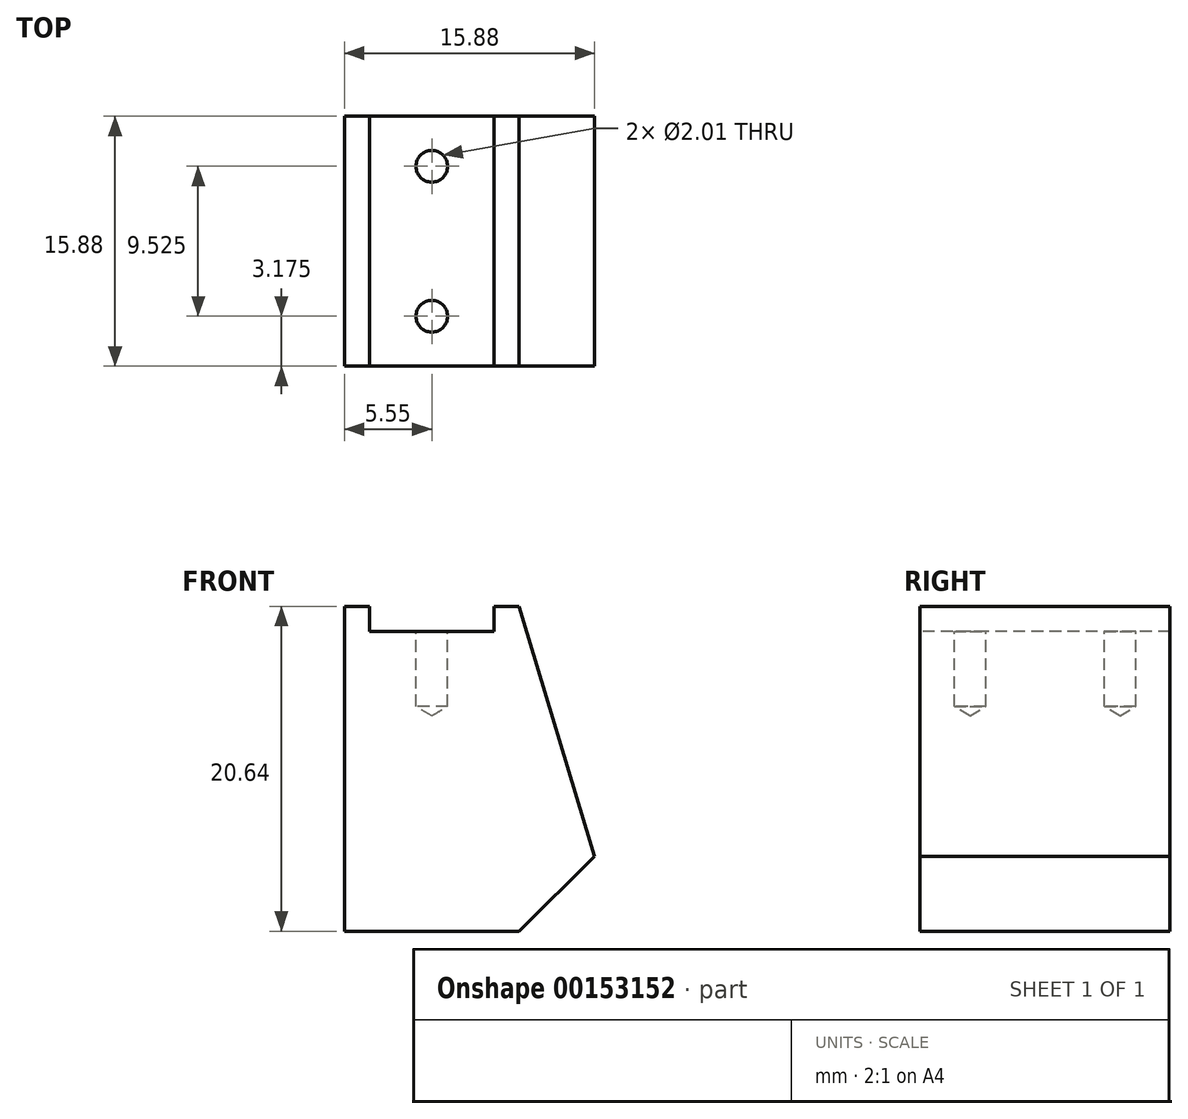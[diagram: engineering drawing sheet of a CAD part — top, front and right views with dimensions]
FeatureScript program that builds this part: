
annotation { "Feature Type Name" : "Feature", "Feature Type Description" : "" }
export const myFeature = defineFeature(function(context is Context, id is Id, definition is map)
    precondition{}
    {
        {
            var Q0;
            Q0=qCreatedBy(makeId("Top.planeOp"),FACE);
            var sketch = newSketch(context, id + "F0", { "sketchPlane" : qUnion([Q0])});
            skLineSegment(sketch, "E0.rect.bottom", {"start": v(7.94, -7.94) * mm, "end": v(-7.94, -7.94) * mm});
            skLineSegment(sketch, "E0.rect.top", {"start": v(7.94, 7.94) * mm, "end": v(-7.94, 7.94) * mm});
            skLineSegment(sketch, "E0.rect.left", {"start": v(7.94, -7.94) * mm, "end": v(7.94, 7.94) * mm});
            skLineSegment(sketch, "E0.rect.right", {"start": v(-7.94, -7.94) * mm, "end": v(-7.94, 7.94) * mm});
            skPoint(sketch, "E0.rect.middle", {"position": v(0, 0) * mm});
            skSolve(sketch);
        }
        {
            var Q0;
            Q0=qSketchRegion(id+"F0",true);
            extrude(context, id + "F1", {"entities" : qUnion([Q0]), "oppositeDirection" : true, "depth" : 20.64 * mm});
        }
        {
            var Q0;
            Q0=makeQuery(id+"F1.opExtrude","CAP_FACE",FACE,{"disambiguationData":[OSD([sQuery(id+"F0.wireOp",EDGE,"E0.rect.bottom"),sQuery(id+"F0.wireOp",EDGE,"E0.rect.top"),sQuery(id+"F0.wireOp",EDGE,"E0.rect.left"),sQuery(id+"F0.wireOp",EDGE,"E0.rect.right")])],"isStart":true});
            var sketch = newSketch(context, id + "F2", { "sketchPlane" : qUnion([Q0])});
            skLineSegment(sketch, "E1.bottom", {"start": v(-6.35, 7.94) * mm, "end": v(1.57, 7.94) * mm});
            skLineSegment(sketch, "E1.top", {"start": v(-6.35, -7.94) * mm, "end": v(1.57, -7.94) * mm});
            skLineSegment(sketch, "E1.left", {"start": v(-6.35, 7.94) * mm, "end": v(-6.35, -7.94) * mm});
            skLineSegment(sketch, "E1.right", {"start": v(1.57, 7.94) * mm, "end": v(1.57, -7.94) * mm});
            skSolve(sketch);
        }
        {
            var Q0;
            Q0=qSketchRegion(id+"F2",true);
            extrude(context, id + "F3", {"entities" : qUnion([Q0]), "operationType" : NewBodyOperationType.REMOVE, "oppositeDirection" : true, "depth" : 1.59 * mm});
        }
        {
            var Q0;
            Q0=makeQuery(id+"F1.opExtrude","SWEPT_BODY",BODY,{"disambiguationData":[OSD([sQuery(id+"F0.wireOp",EDGE,"E0.rect.bottom"),sQuery(id+"F0.wireOp",EDGE,"E0.rect.top"),sQuery(id+"F0.wireOp",EDGE,"E0.rect.left"),sQuery(id+"F0.wireOp",EDGE,"E0.rect.right")])]});
            var Q1;
            {var subQ0=sQuery(id+"F0.wireOp",EDGE,"E0.rect.bottom");var subQ1=sQuery(id+"F0.wireOp",EDGE,"E0.rect.left");Q1=makeQuery(id+"F3.boolean.opBoolean","SPLIT",EDGE,{"disambiguationData":[TD([makeQuery(id+"F1.opExtrude","SWEPT_FACE",FACE,{"disambiguationData":[OSD([subQ1])]})])],"derivedFrom":makeQuery(id+"F1.opExtrude","CAP_EDGE",EDGE,{"disambiguationData":[OSD([subQ0])],"isStart":true})});}
            transform(context, id + "F4", {"entities" : qUnion([Q0]), "transformType" : TransformType.TRANSLATION_DISTANCE, "transformDirection" : qUnion([Q1]), "distance" : 7.94 * mm, "oppositeDirection" : true, "makeCopy" : false});
        }
        {
            var Q0;
            Q0=makeQuery(id+"F1.opExtrude","SWEPT_BODY",BODY,{"disambiguationData":[OSD([sQuery(id+"F0.wireOp",EDGE,"E0.rect.bottom"),sQuery(id+"F0.wireOp",EDGE,"E0.rect.top"),sQuery(id+"F0.wireOp",EDGE,"E0.rect.left"),sQuery(id+"F0.wireOp",EDGE,"E0.rect.right")])]});
            var Q1;
            Q1=makeQuery(id+"F1.opExtrude","CAP_EDGE",EDGE,{"disambiguationData":[OSD([sQuery(id+"F0.wireOp",EDGE,"E0.rect.right")])],"isStart":true});
            transform(context, id + "F5", {"entities" : qUnion([Q0]), "transformType" : TransformType.TRANSLATION_DISTANCE, "transformDirection" : qUnion([Q1]), "distance" : 7.94 * mm, "makeCopy" : false});
        }
        {
            var Q0;
            Q0=makeQuery(id+"F3.boolean.opBoolean","COPY",FACE,{"derivedFrom":makeQuery(id+"F3.opExtrude","CAP_FACE",FACE,{"disambiguationData":[OSD([sQuery(id+"F2.wireOp",EDGE,"E1.bottom"),sQuery(id+"F2.wireOp",EDGE,"E1.top"),sQuery(id+"F2.wireOp",EDGE,"E1.left"),sQuery(id+"F2.wireOp",EDGE,"E1.right")])],"isStart":false})});
            var sketch = newSketch(context, id + "F6", { "sketchPlane" : qUnion([Q0])});
            skPoint(sketch, "E2", {"position": v(5.55, 12.7) * mm});
            skPoint(sketch, "E2.positionSnap0", {"position": v(5.55, 15.88) * mm});
            skPoint(sketch, "E3", {"position": v(5.55, 3.17) * mm});
            skLineSegment(sketch, "E4", {"start": v(-3.05, 7.94) * mm, "end": v(9.51, 7.94) * mm, "construction": true});
            skPoint(sketch, "E5", {"position": v(1.59, 7.94) * mm});
            skSolve(sketch);
        }
        {
            var Q0;
            Q0=sQuery(id+"F6.wireOp",VERTEX,"E2");
            var Q1;
            Q1=sQuery(id+"F6.wireOp",VERTEX,"E3");
            var Q2;
            Q2=makeQuery(id+"F1.opExtrude","SWEPT_BODY",BODY,{"disambiguationData":[OSD([sQuery(id+"F0.wireOp",EDGE,"E0.rect.bottom"),sQuery(id+"F0.wireOp",EDGE,"E0.rect.top"),sQuery(id+"F0.wireOp",EDGE,"E0.rect.left"),sQuery(id+"F0.wireOp",EDGE,"E0.rect.right")])]});
            hole(context, id + "F7", {"style" : HoleStyle.SIMPLE, "holeDiameter" : 2 * mm, "endStyle" : HoleEndStyle.BLIND, "holeDepth" : 4.76 * mm, "locations" : qUnion([Q0, Q1]), "scope" : qUnion([Q2])});
        }
        {
            var Q0;
            Q0=makeQuery(id+"F1.opExtrude","SWEPT_FACE",FACE,{"disambiguationData":[OSD([sQuery(id+"F0.wireOp",EDGE,"E0.rect.bottom")])]});
            var sketch = newSketch(context, id + "F8", { "sketchPlane" : qUnion([Q0])});
            skLineSegment(sketch, "E6", {"start": v(11.1, 0) * mm, "end": v(15.88, -15.88) * mm});
            skLineSegment(sketch, "E7", {"start": v(15.88, -15.88) * mm, "end": v(15.88, 0) * mm});
            skLineSegment(sketch, "E8", {"start": v(15.88, 0) * mm, "end": v(11.1, 0) * mm});
            skSolve(sketch);
        }
        {
            var Q0;
            Q0=qSketchRegion(id+"F8",true);
            extrude(context, id + "F9", {"entities" : qUnion([Q0]), "operationType" : NewBodyOperationType.REMOVE, "endBound" : BoundingType.THROUGH_ALL, "oppositeDirection" : true, "depth" : 25.4 * mm});
        }
        {
            var Q0;
            Q0=makeQuery(id+"F1.opExtrude","SWEPT_FACE",FACE,{"disambiguationData":[OSD([sQuery(id+"F0.wireOp",EDGE,"E0.rect.bottom")])]});
            var sketch = newSketch(context, id + "F10", { "sketchPlane" : qUnion([Q0])});
            skLineSegment(sketch, "E9", {"start": v(15.88, -15.88) * mm, "end": v(11.1, -20.64) * mm});
            skLineSegment(sketch, "E10", {"start": v(11.1, -20.64) * mm, "end": v(15.88, -20.64) * mm});
            skLineSegment(sketch, "E11", {"start": v(15.88, -20.64) * mm, "end": v(15.88, -15.88) * mm});
            skSolve(sketch);
        }
        {
            var Q0;
            Q0=qSketchRegion(id+"F10",true);
            extrude(context, id + "F11", {"entities" : qUnion([Q0]), "operationType" : NewBodyOperationType.REMOVE, "endBound" : BoundingType.THROUGH_ALL, "oppositeDirection" : true, "depth" : 25.4 * mm});
        }
    });
